# Revit family: Pendelaufhänger M 8
name_source: partatom
category: HLS-Bauteile
revit_build: Autodesk Revit 2017 (Build: 20190507_1515(x64)
units: mm (PartAtom-declared; Revit-internal decimal feet)

## family parameters
Arbeitsebenenbasiert = Ja
Beim Laden mit Abzugskörper schneiden = Nein
Bemaßung runder Anschluss = Durchmesser verwenden
Gemeinsam genutzt = Ja
Immer vertikal = Nein
Raumberechnungspunkt = Nein
Teiletyp = Normal

## types (1)
- Pendelaufhänger M 8/M 8
    Artikelnummer = 0784031
    B = 55 mm  [stored 0.180446 ft]
    C = 15 mm  [stored 0.0492126 ft]
    EAN = 4250928418913
    Fabrikat = MEFA
    Firma = MEFA Befestigungs- und Montagesysteme GmbH
    Gewicht = 0.11 kg
    Gewicht pro Bauteil = 0.11 kg
    Gewinde = M8-M8
    Gewindetyp = AG-AG
    Höhe = 44 mm
    Kurztext1 = Pendelaufhänger 15°
    Kurztext2 = AG-AG M8-M8
    L = 21 mm  [stored 0.0688976 ft]
    Länge Gewinde = 22 mm  [stored 0.0721785 ft]
    Material = Stahl
    Materialname = S235
    Mengeneinheit = St
    Mutter DIN928 = Mutter DIN 928 : Mutter DIN 928 M 8
    Oberflaeche = galvanisch verzinkt
    Pendelschraube = Pendelschraube : Pendelschraube M 8
    Pendelwinkel = 15
    Sechskantmutter = MEFA Sechskantmutter : Sechskantmutter M 8
    Unterlegscheibe = Unterlegscheibe für M 8 : Unterlegscheibe  8,4x24x2,0
    Vorgabe-Ansicht = 1219 mm
    max. zul. Last = 2.50 kN
    vpe = 50 St

note: [stored X ft] marks values corroborated as IEEE doubles in the binary element streams (Revit-internal decimal feet)

## geometry (parser evidence)
native form markers: Sweep x3
no freeform markers — native parametric forms only
